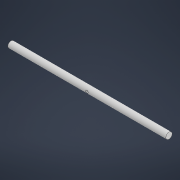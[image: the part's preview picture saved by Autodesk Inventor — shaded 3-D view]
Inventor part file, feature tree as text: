
AUTODESK INVENTOR PART (.ipt)
format: ipt  version: 2022 (Build 260153000, 153)  size: 101,888 bytes
history: native  units: in
note: dims shown in document units (in); Inventor stores cm internally (conversion verified against a paired STEP export)
features: extrude x1, fillet x1, sketch x1
ambient origin geometry x8: Origin, YZ Plane, XZ Plane, XY Plane, X Axis, Y Axis, Z Axis, Center Point
bodies: Solid1 (feature_tree)
feature tree (3):
  extrude  "Extrusion1"  Depth=0.5in
  fillet  "Fillet1"  Radius=0.3937in
  sketch  "Sketch1"  dims[d0=25.5906in d1=1.0in d2=0.3937in d3=1.0in d4=0.0in d5=0.5in]
